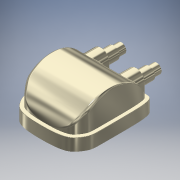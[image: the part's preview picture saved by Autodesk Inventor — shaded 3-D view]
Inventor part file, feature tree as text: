
AUTODESK INVENTOR PART (.ipt)
format: ipt  version: 2016 (Build 200138000, 138)  size: 914,432 bytes
history: native  units: in
note: dims shown in document units (in); Inventor stores cm internally (conversion verified against a paired STEP export)
features: extrude x16, sketch x16, projected_geometry x16, fillet x9, mirror x3, plane x2, hole x2
ambient origin geometry x8: Origin, YZ Plane, XZ Plane, XY Plane, X Axis, Y Axis, Z Axis, Center Point
bodies: Solid1 (feature_tree)
feature tree (64):
  extrude  "Extrusion1"  Depth=3.5433in
  extrude  "Extrusion2"  Depth=0.1575in
  extrude  "Extrusion3"  Depth=1.2402in TaperAngle=0.0deg
  extrude  "Extrusion5"  Depth=0.748in
  mirror  "Mirror3"
  fillet  "Fillet8"  Radius=0.8661in
  fillet  "Fillet9"  Radius=1.6929in
  fillet  "Fillet10"  [1 undecoded]
  extrude  "Extrusion6"  Depth=0.1969in
  extrude  "Extrusion7"  Depth=0.063in
  extrude  "Extrusion8"  Depth=0.5512in
  mirror  "Mirror4"
  extrude  "Extrusion9"  Depth=0.3937in TaperAngle=0.0deg
  extrude  "Extrusion10"  Depth=0.3543in TaperAngle=0.0deg
  plane  "Work Plane2"
  extrude  "Extrusion11"  Depth=0.0787in TaperAngle=0.0deg
  extrude  "Extrusion12"  Depth=0.5906in
  fillet  "Fillet11"  Radius=0.7874in
  hole  "Hole2"  [1 undecoded]
  sketch  "Sketch16"  dims[d58=0.2559in d59=0.0in d60=1.5748in]
  extrude  "Extrusion13"  Depth=1.5748in
  extrude  "Extrusion14"  Depth=0.3543in
  extrude  "Extrusion15"  Depth=0.1181in
  hole  "Hole3"  [1 undecoded]
  fillet  "Fillet12"  Radius=2.3622in
  fillet  "Fillet13"  Radius=2.3622in
  fillet  "Fillet14"  Radius=0.0394in
  fillet  "Fillet15"  Radius=0.0787in
  extrude  "Extrusion16"  Depth=0.0157in
  extrude  "Extrusion17"  Depth=0.0787in
  fillet  "Fillet16"  Radius=0.0787in
  mirror  "Mirror5"
  plane  "Work Plane3"
  sketch  "Sketch1"  dims[d0=3.0709in d1=3.5433in]
  sketch  "Sketch2"  dims[d2=0.5512in d3=0.0in d4=0.1575in]
  projected_geometry  "Projected Loop2"
  sketch  "Sketch4"  dims[d5=1.378in d6=0.0in d7=1.2402in d8=0.0in]
  projected_geometry  "Projected Loop3"
  sketch  "Sketch5"  dims[d20=1.5748in d31=0.748in d33=0.8661in d34=1.6929in d35=0.0in d36=0.0in]
  sketch  "Sketch7"  dims[d37=0.1969in d38=0.1969in]
  sketch  "Sketch8"  dims[d39=0.0in d40=0.063in]
  sketch  "Sketch9"  dims[d41=0.063in d42=0.5512in]
  sketch  "Sketch10"  dims[d43=0.3937in d44=0.5512in d45=0.0in]
  sketch  "Sketch11"  dims[d46=0.0591in d47=0.3543in d48=0.0in]
  projected_geometry  "Projected Loop4"
  sketch  "Sketch12"  dims[d49=0.0787in d50=0.7874in d51=0.0in]
  projected_geometry  "Projected Loop5"
  sketch  "Sketch14"  dims[d52=1.811in d53=0.5906in d54=0.7874in d55=0.0in]
  sketch  "Sketch15"  dims[d56=1.9685in d57=1.9685in]
  projected_geometry  "Projected Loop10"
  projected_geometry  "Projected Loop11"
  sketch  "Sketch17"  dims[d61=1.5748in d62=0.3543in]
  projected_geometry  "Projected Loop12"
  projected_geometry  "Projected Loop13"
  projected_geometry  "Projected Loop14"
  projected_geometry  "Projected Loop15"
  sketch  "Sketch18"  dims[d63=0.1476in d64=0.0in d72=0.1181in]
  sketch  "Sketch20"  dims[d73=0.0906in d74=0.0in d75=0.1969in d76=2.3622in d77=2.3622in d78=0.1181in d79=0.2362in d80=0.1575in d81=0.0787in d82=90.0deg d83=0.4724in d84=0.8108in d85=0.0394in d86=0.0787in d87=0.0in d88=0.1181in d89=0.0787in d90=0.0787in d91=0.0787in d92=0.0787in d93=0.4547in d94=0.0in d95=0.0787in d96=0.0in d98=-0.0512in d99=0.1181in d100=0.2362in d101=0.1575in d102=0.0787in d103=90.0deg d104=0.3937in d105=0.8108in d106=0.0197in d107=0.0197in d108=0.0157in d109=0.0157in d110=0.0787in d111=0.6299in d112=1.1417in d113=0.6406in d114=0.0in d116=0.0236in d117=0.0787in d118=0.0394in d119=0.4134in d120=0.0in d121=0.0157in d122=-0.4921in]
  projected_geometry  "Projected Loop16"
  projected_geometry  "Project Cut Edges3"
  projected_geometry  "Project Cut Edges4"
  projected_geometry  "Project Cut Edges5"
  projected_geometry  "Project Cut Edges6"
  projected_geometry  "Project Cut Edges7"
note: 3 required parameter values undecoded (feature->parameter linkage not recoverable at this tier; creation-order binding heuristic only, values carry confidence <= 0.55)
